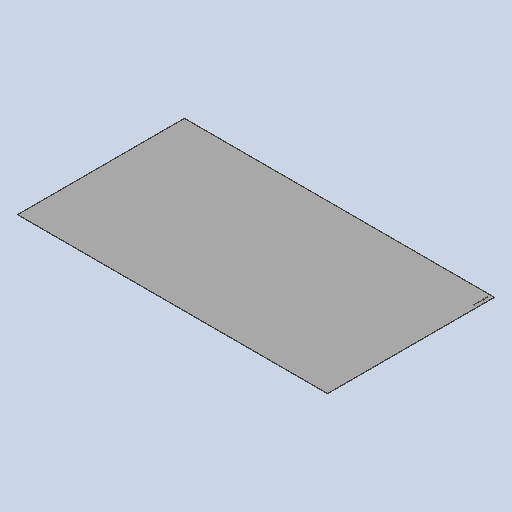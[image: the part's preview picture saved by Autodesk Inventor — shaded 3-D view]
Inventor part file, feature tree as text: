
AUTODESK INVENTOR PART (.ipt)
format: ipt  version: 2025 (Build 290162010, 162A)  size: 169,984 bytes
history: native  units: mm
features: other x3, sketch x2, sheet_metal_op x1
ambient origin geometry x8: Origin, YZ Plane, XZ Plane, XY Plane, X Axis, Y Axis, Z Axis, Center Point
bodies: Solid1 (feature_tree)
feature tree (6):
  sheet_metal_op  "Face1"
  other  "Mark1"
  sketch  "Sketch1"  dims[d0=2748.0mm]
  other  "Plate1"
  sketch  "Sketch5"  dims[d1=1479.0mm d2=3.0mm d26=200.0mm d27=15.0mm d28=25.0mm d29=25.0mm]
  other  "Definition1"
